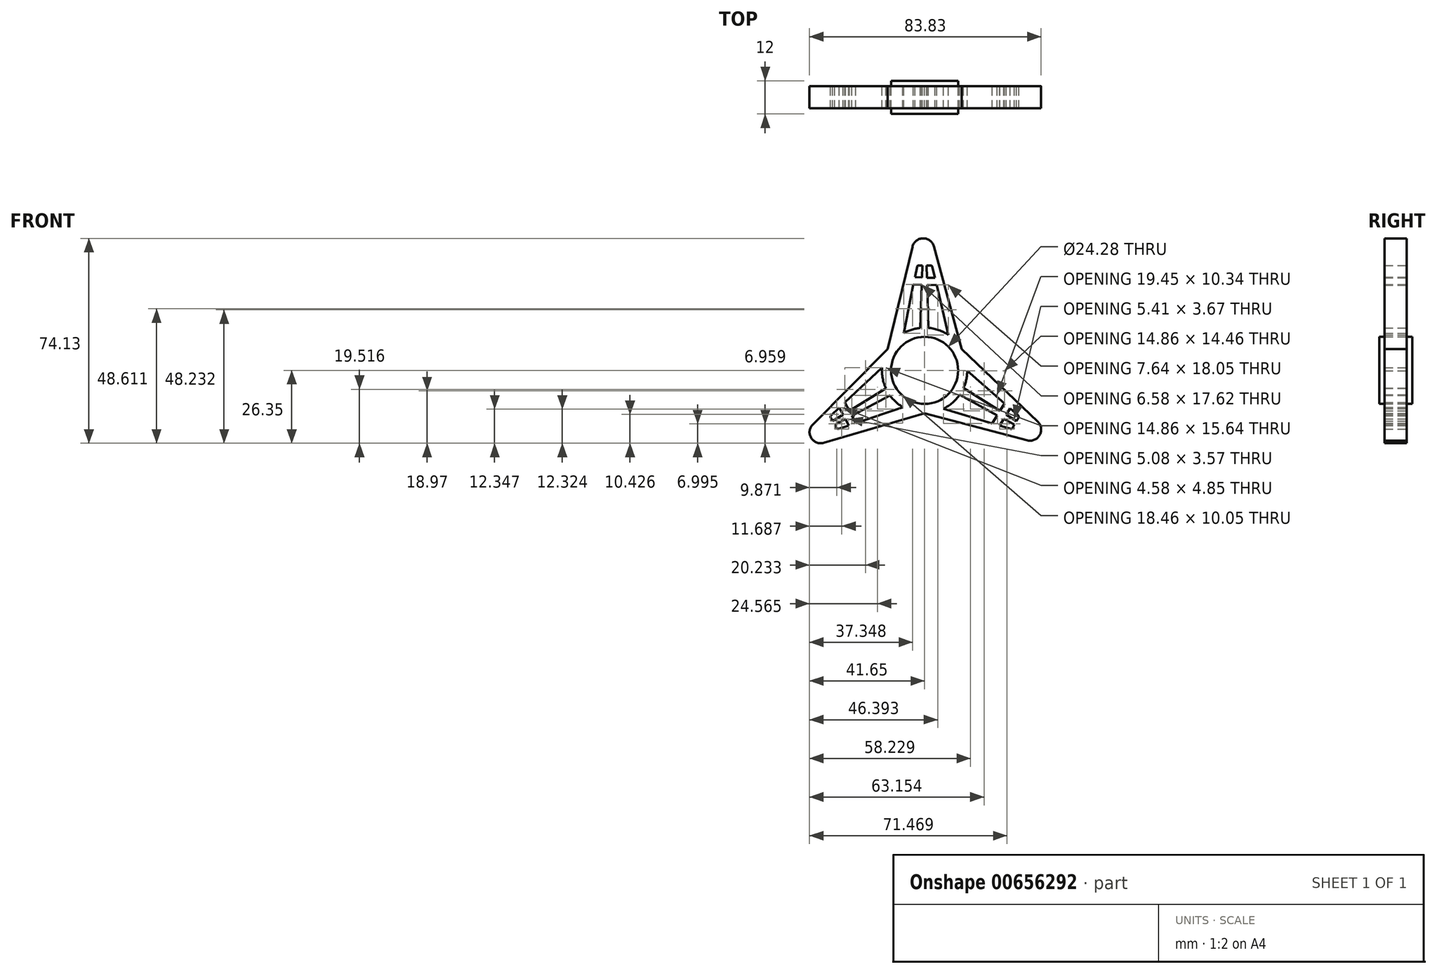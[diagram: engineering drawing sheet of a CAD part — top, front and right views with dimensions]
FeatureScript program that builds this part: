
annotation { "Feature Type Name" : "Feature", "Feature Type Description" : "" }
export const myFeature = defineFeature(function(context is Context, id is Id, definition is map)
    precondition{}
    {
        {
            var Q0;
            Q0=qCreatedBy(makeId("Front.planeOp"),FACE);
            var sketch = newSketch(context, id + "F0", { "sketchPlane" : qUnion([Q0])});
            skCircle(sketch, "E0", {"center": v(0, 0) * mm, "radius": 12.14 * mm});
            skCircle(sketch, "E1", {"center": v(0, 0) * mm, "radius": 15.45 * mm});
            skLineSegment(sketch, "E2", {"start": v(-13.45, 7.6) * mm, "end": v(-4.42, 44.72) * mm});
            skLineSegment(sketch, "E3", {"start": v(3.33, 44.83) * mm, "end": v(13.45, 7.6) * mm});
            skLineSegment(sketch, "E4.1.2", {"start": v(-39.55, -18.7) * mm, "end": v(-13.45, 7.6) * mm});
            skLineSegment(sketch, "E4.2.1", {"start": v(13.45, 7.6) * mm, "end": v(40.07, -17.81) * mm});
            skPoint(sketch, "E4.center", {"position": v(0, -0.17) * mm});
            skPoint(sketch, "E5.newPointA", {"position": v(-4.75, 43.35) * mm});
            skPoint(sketch, "E5.newPointB", {"position": v(3.73, 43.35) * mm});
            skArc(sketch, "E5.filletArc", {"start": v(3.33, 44.83) * mm, "mid": v(-0.59, 47.78) * mm, "end": v(-4.42, 44.72) * mm});
            skArc(sketch, "E6.1.0", {"start": v(-40.49, -19.53) * mm, "mid": v(-41.08, -24.4) * mm, "end": v(-36.52, -26.19) * mm});
            skLineSegment(sketch, "E6.1.2", {"start": v(0.15, -15.45) * mm, "end": v(-36.52, -26.19) * mm});
            skArc(sketch, "E6.2.0", {"start": v(37.16, -25.3) * mm, "mid": v(41.67, -23.38) * mm, "end": v(40.94, -18.54) * mm});
            skLineSegment(sketch, "E6.2.1", {"start": v(37.16, -25.3) * mm, "end": v(-0.15, -15.45) * mm});
            skLineSegment(sketch, "E7", {"start": v(-7.6, 13.45) * mm, "end": v(-2.77, 37.48) * mm});
            skLineSegment(sketch, "E8", {"start": v(-2.15, 37.99) * mm, "end": v(2.17, 37.99) * mm});
            skLineSegment(sketch, "E9", {"start": v(2.79, 37.5) * mm, "end": v(8.56, 12.86) * mm});
            skLineSegment(sketch, "E10", {"start": v(-0.78, 37.99) * mm, "end": v(-1.52, 15.37) * mm});
            skLineSegment(sketch, "E11", {"start": v(0.75, 37.99) * mm, "end": v(1.32, 15.4) * mm});
            skPoint(sketch, "E12.visualSharp", {"position": v(-2.67, 37.99) * mm});
            skArc(sketch, "E12.filletArc", {"start": v(-2.15, 37.99) * mm, "mid": v(-2.55, 37.84) * mm, "end": v(-2.77, 37.48) * mm});
            skPoint(sketch, "E13.visualSharp", {"position": v(2.67, 37.99) * mm});
            skArc(sketch, "E13.filletArc", {"start": v(2.79, 37.5) * mm, "mid": v(2.56, 37.85) * mm, "end": v(2.17, 37.99) * mm});
            skLineSegment(sketch, "E14.1.1", {"start": v(-33.27, -18.35) * mm, "end": v(-13.99, -6.56) * mm});
            skPoint(sketch, "E14.1.2", {"position": v(-34.23, -16.68) * mm});
            skLineSegment(sketch, "E14.1.3", {"start": v(-33.87, -16.34) * mm, "end": v(-15.42, 0.98) * mm});
            skPoint(sketch, "E14.1.4", {"position": v(-35.17, -25.8) * mm});
            skPoint(sketch, "E14.1.5", {"position": v(-39.4, -18.45) * mm});
            skPoint(sketch, "E14.1.6", {"position": v(-31.56, -21.3) * mm});
            skLineSegment(sketch, "E14.1.7", {"start": v(-7.85, -13.3) * mm, "end": v(-31.07, -21.14) * mm});
            skLineSegment(sketch, "E14.1.8", {"start": v(-32.5, -19.67) * mm, "end": v(-12.55, -9) * mm});
            skLineSegment(sketch, "E14.1.9", {"start": v(-31.82, -20.86) * mm, "end": v(-33.98, -17.11) * mm});
            skArc(sketch, "E14.1.10", {"start": v(-31.82, -20.86) * mm, "mid": v(-31.5, -21.13) * mm, "end": v(-31.07, -21.14) * mm});
            skArc(sketch, "E14.1.11", {"start": v(-33.87, -16.34) * mm, "mid": v(-34.06, -16.7) * mm, "end": v(-33.98, -17.11) * mm});
            skLineSegment(sketch, "E14.2.1", {"start": v(32.52, -19.64) * mm, "end": v(12.67, -8.84) * mm});
            skPoint(sketch, "E14.2.2", {"position": v(31.56, -21.3) * mm});
            skLineSegment(sketch, "E14.2.3", {"start": v(31.08, -21.16) * mm, "end": v(6.85, -13.84) * mm});
            skPoint(sketch, "E14.2.4", {"position": v(39.92, -17.56) * mm});
            skPoint(sketch, "E14.2.5", {"position": v(35.68, -24.9) * mm});
            skPoint(sketch, "E14.2.6", {"position": v(34.23, -16.68) * mm});
            skLineSegment(sketch, "E14.2.7", {"start": v(15.45, -0.15) * mm, "end": v(33.84, -16.34) * mm});
            skLineSegment(sketch, "E14.2.8", {"start": v(33.29, -18.32) * mm, "end": v(14.07, -6.37) * mm});
            skLineSegment(sketch, "E14.2.9", {"start": v(33.97, -17.13) * mm, "end": v(31.81, -20.87) * mm});
            skArc(sketch, "E14.2.10", {"start": v(33.97, -17.13) * mm, "mid": v(34.05, -16.7) * mm, "end": v(33.84, -16.34) * mm});
            skArc(sketch, "E14.2.11", {"start": v(31.08, -21.16) * mm, "mid": v(31.5, -21.14) * mm, "end": v(31.81, -20.87) * mm});
            skLineSegment(sketch, "E14.2.12", {"start": v(13.3, 7.85) * mm, "end": v(40.94, -18.54) * mm});
            skLineSegment(sketch, "E15.1.0", {"start": v(-40.49, -19.53) * mm, "end": v(-13.3, 7.85) * mm});
            skLineSegment(sketch, "E16", {"start": v(-30.85, -13.5) * mm, "end": v(-27.42, -19.9) * mm});
            skLineSegment(sketch, "E17", {"start": v(-28.85, -11.62) * mm, "end": v(-24.88, -19.05) * mm});
            skLineSegment(sketch, "E18.1.0", {"start": v(24.5, -19.17) * mm, "end": v(28.94, -12.02) * mm});
            skLineSegment(sketch, "E18.1.1", {"start": v(27.12, -19.96) * mm, "end": v(30.95, -13.8) * mm});
            skLineSegment(sketch, "E18.2.0", {"start": v(4.36, 30.8) * mm, "end": v(-4.06, 31.07) * mm});
            skLineSegment(sketch, "E18.2.1", {"start": v(3.73, 33.46) * mm, "end": v(-3.53, 33.7) * mm});
            skSolve(sketch);
        }
        {
            var Q0;
            Q0 = qSketchRegion(id + "F0", true);
            var Q1;
            {var subQ0=sQuery(id+"F0.wireOp",EDGE,"E14.1.1");Q1=makeQuery(id+"F0.imprint","IMPRINT",FACE,{"disambiguationData":[TD([[makeQuery(id+"F0.imprint","IMPRINT",EDGE,{"derivedFrom":subQ0}),-1.0]])]});}
            var Q2;
            Q2=makeQuery(id+"F0.imprint","IMPRINT",FACE,{"disambiguationData":[TD([[makeQuery(id+"F0.imprint","IMPRINT",EDGE,{"derivedFrom":sQuery(id+"F0.wireOp",EDGE,"E0")}),-1.0]])]});
            var Q3;
            {var subQ0=sQuery(id+"F0.wireOp",EDGE,"E10");Q3=makeQuery(id+"F0.imprint","IMPRINT",FACE,{"disambiguationData":[TD([[makeQuery(id+"F0.imprint","IMPRINT",EDGE,{"derivedFrom":subQ0}),1.0]])]});}
            var Q4;
            {var subQ0=sQuery(id+"F0.wireOp",EDGE,"E14.2.1");Q4=makeQuery(id+"F0.imprint","IMPRINT",FACE,{"disambiguationData":[TD([[makeQuery(id+"F0.imprint","IMPRINT",EDGE,{"derivedFrom":subQ0}),-1.0]])]});}
            var Q5;
            {var subQ0=sQuery(id+"F0.wireOp",EDGE,"E18.2.0");var subQ1=sQuery(id+"F0.wireOp",EDGE,"E9");var subQ2=makeQuery(id+"F0.imprint","INTERSECT",VERTEX,{"derivedFrom":[subQ1,subQ0]});Q5=makeQuery(id+"F0.imprint","IMPRINT",FACE,{"disambiguationData":[TD([[makeQuery(id+"F0.imprint","IMPRINT",EDGE,{"disambiguationData":[TD([[subQ2,1.0]])],"derivedFrom":subQ1}),-1.0]])]});}
            var Q6;
            {var subQ0=sQuery(id+"F0.wireOp",EDGE,"E18.2.0");var subQ1=sQuery(id+"F0.wireOp",EDGE,"E7");var subQ2=makeQuery(id+"F0.imprint","INTERSECT",VERTEX,{"derivedFrom":[subQ1,subQ0]});Q6=makeQuery(id+"F0.imprint","IMPRINT",FACE,{"disambiguationData":[TD([[makeQuery(id+"F0.imprint","IMPRINT",EDGE,{"disambiguationData":[TD([[subQ2,-1.0]])],"derivedFrom":subQ1}),-1.0]])]});}
            var Q7;
            {var subQ0=sQuery(id+"F0.wireOp",EDGE,"E16");var subQ1=sQuery(id+"F0.wireOp",EDGE,"E14.1.1");var subQ2=makeQuery(id+"F0.imprint","INTERSECT",VERTEX,{"derivedFrom":[subQ1,subQ0]});Q7=makeQuery(id+"F0.imprint","IMPRINT",FACE,{"disambiguationData":[TD([[makeQuery(id+"F0.imprint","IMPRINT",EDGE,{"disambiguationData":[TD([[subQ2,-1.0]])],"derivedFrom":subQ1}),1.0]])]});}
            var Q8;
            {var subQ0=sQuery(id+"F0.wireOp",EDGE,"E16");var subQ1=sQuery(id+"F0.wireOp",EDGE,"E14.1.7");var subQ2=makeQuery(id+"F0.imprint","INTERSECT",VERTEX,{"derivedFrom":[subQ1,subQ0]});Q8=makeQuery(id+"F0.imprint","IMPRINT",FACE,{"disambiguationData":[TD([[makeQuery(id+"F0.imprint","IMPRINT",EDGE,{"disambiguationData":[TD([[subQ2,1.0]])],"derivedFrom":subQ1}),-1.0]])]});}
            var Q9;
            {var subQ0=sQuery(id+"F0.wireOp",EDGE,"E18.1.0");var subQ1=sQuery(id+"F0.wireOp",EDGE,"E14.2.7");var subQ2=makeQuery(id+"F0.imprint","INTERSECT",VERTEX,{"derivedFrom":[subQ1,subQ0]});Q9=makeQuery(id+"F0.imprint","IMPRINT",FACE,{"disambiguationData":[TD([[makeQuery(id+"F0.imprint","IMPRINT",EDGE,{"disambiguationData":[TD([[subQ2,-1.0]])],"derivedFrom":subQ1}),-1.0]])]});}
            var Q10;
            {var subQ0=sQuery(id+"F0.wireOp",EDGE,"E18.1.1");var subQ1=sQuery(id+"F0.wireOp",EDGE,"E14.2.1");var subQ2=makeQuery(id+"F0.imprint","INTERSECT",VERTEX,{"derivedFrom":[subQ1,subQ0]});Q10=makeQuery(id+"F0.imprint","IMPRINT",FACE,{"disambiguationData":[TD([[makeQuery(id+"F0.imprint","IMPRINT",EDGE,{"disambiguationData":[TD([[subQ2,-1.0]])],"derivedFrom":subQ1}),1.0]])]});}
            extrude(context, id + "F1", {"entities" : qUnion([Q0, Q1, Q2, Q3, Q4, Q5, Q6, Q7, Q8, Q9, Q10]), "depth" : 8 * mm, "offsetDistance" : 25 * mm});
        }
        {
            var Q0;
            Q0=makeQuery(id+"F0.imprint","IMPRINT",FACE,{"disambiguationData":[TD([[makeQuery(id+"F0.imprint","IMPRINT",EDGE,{"derivedFrom":sQuery(id+"F0.wireOp",EDGE,"E0")}),1.0]])]});
            extrude(context, id + "F2", {"entities" : qUnion([Q0]), "oppositeDirection" : true, "depth" : 2 * mm, "offsetDistance" : 25 * mm});
        }
        {
            var Q0;
            Q0=makeQuery(id+"F0.imprint","IMPRINT",FACE,{"disambiguationData":[TD([[makeQuery(id+"F0.imprint","IMPRINT",EDGE,{"derivedFrom":sQuery(id+"F0.wireOp",EDGE,"E0")}),1.0]])]});
            extrude(context, id + "F3", {"entities" : qUnion([Q0]), "depth" : 10 * mm, "offsetDistance" : 25 * mm});
        }
    });
